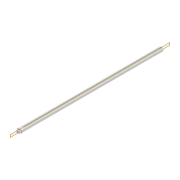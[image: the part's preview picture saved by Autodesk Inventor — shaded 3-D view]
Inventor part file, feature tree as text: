
AUTODESK INVENTOR PART (.ipt)
format: ipt  version: 2022 (Build 260153000, 153)  size: 90,624 bytes
history: native  units: mm
features: extrude x1, sketch x1
ambient origin geometry x8: Origin, YZ Plane, XZ Plane, XY Plane, X Axis, Y Axis, Z Axis, Center Point
bodies: Solid1 (feature_tree)
feature tree (2):
  extrude  "Extrusion1"  Depth=300.0mm
  sketch  "Sketch1"  dims[d0=8.0mm d1=300.0mm d2=4.2mm d3=4.2mm d4=10.0mm d5=5.0mm d6=0.0mm]
